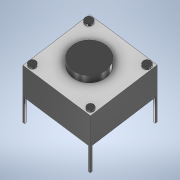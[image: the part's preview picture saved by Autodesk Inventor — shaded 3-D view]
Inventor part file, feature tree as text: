
AUTODESK INVENTOR PART (.ipt)
format: ipt  version: 2022 (Build 260153070, 153G)  size: 155,136 bytes
history: native  units: in
note: dims shown in document units (in); Inventor stores cm internally (conversion verified against a paired STEP export)
features: extrude x4, sketch x4
ambient origin geometry x8: Origin, YZ Plane, XZ Plane, XY Plane, X Axis, Y Axis, Z Axis, Center Point
bodies: Solid1 (feature_tree)
feature tree (8):
  extrude  "Extrusion1"  Depth=0.6in
  extrude  "Extrusion2"  Depth=0.07in TaperAngle=0.0deg
  extrude  "Extrusion3"  Depth=0.25in TaperAngle=0.0deg
  extrude  "Extrusion4"  [1 undecoded]
  sketch  "Sketch1"  dims[d0=0.6in d1=0.6in]
  sketch  "Sketch2"  dims[d2=0.3in d3=0.0in d4=0.07in d5=0.0in]
  sketch  "Sketch3"  dims[d6=0.02in d7=0.0in d8=0.25in d9=0.0in]
  sketch  "Sketch4"
note: 1 required parameter value undecoded (feature->parameter linkage not recoverable at this tier; creation-order binding heuristic only, values carry confidence <= 0.55)
